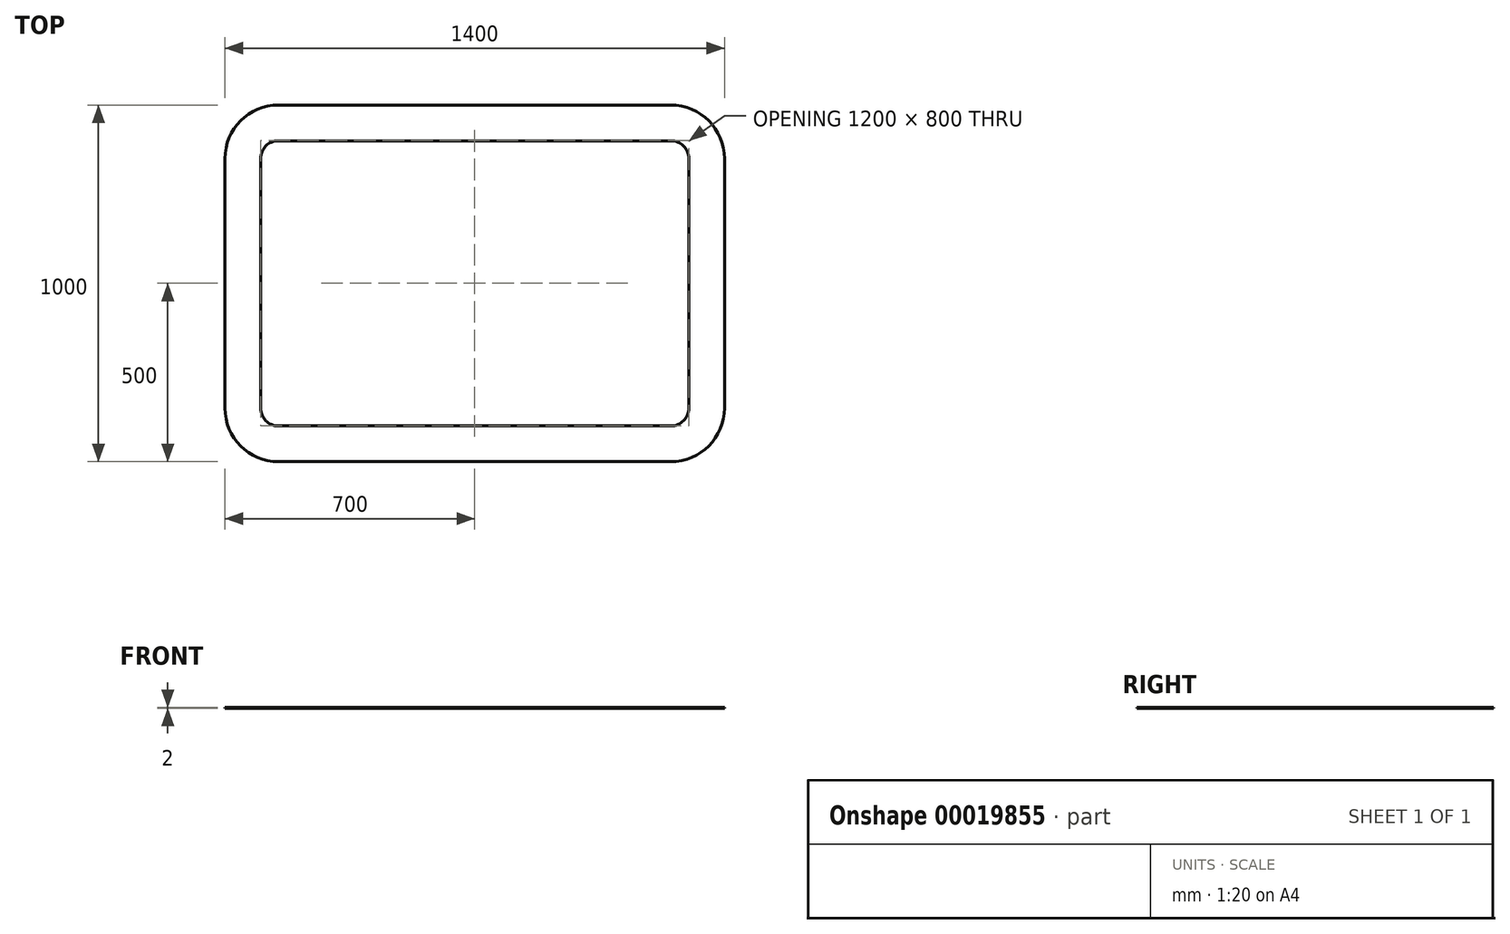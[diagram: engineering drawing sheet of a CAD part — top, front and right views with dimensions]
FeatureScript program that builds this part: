
annotation { "Feature Type Name" : "Feature", "Feature Type Description" : "" }
export const myFeature = defineFeature(function(context is Context, id is Id, definition is map)
    precondition{}
    {
        {
            var Q0;
            Q0=qCreatedBy(makeId("Top.planeOp"),FACE);
            var sketch = newSketch(context, id + "F0", { "sketchPlane" : qUnion([Q0])});
            skLineSegment(sketch, "E0.rect.bottom", {"start": v(-550, 400) * mm, "end": v(550, 400) * mm});
            skLineSegment(sketch, "E0.rect.top", {"start": v(-550, -400) * mm, "end": v(550, -400) * mm});
            skLineSegment(sketch, "E0.rect.left", {"start": v(-600, 350) * mm, "end": v(-600, -350) * mm});
            skLineSegment(sketch, "E0.rect.right", {"start": v(600, 350) * mm, "end": v(600, -350) * mm});
            skPoint(sketch, "E0.rect.middle", {"position": v(0, 0) * mm});
            skPoint(sketch, "E1.visualSharp", {"position": v(-600, 400) * mm});
            skArc(sketch, "E1.filletArc", {"start": v(-550, 400) * mm, "mid": v(-585.36, 385.36) * mm, "end": v(-600, 350) * mm});
            skPoint(sketch, "E2.visualSharp", {"position": v(-600, -400) * mm});
            skArc(sketch, "E2.filletArc", {"start": v(-600, -350) * mm, "mid": v(-585.36, -385.36) * mm, "end": v(-550, -400) * mm});
            skPoint(sketch, "E3.visualSharp", {"position": v(600, -400) * mm});
            skArc(sketch, "E3.filletArc", {"start": v(550, -400) * mm, "mid": v(585.36, -385.36) * mm, "end": v(600, -350) * mm});
            skPoint(sketch, "E4.visualSharp", {"position": v(600, 400) * mm});
            skArc(sketch, "E4.filletArc", {"start": v(600, 350) * mm, "mid": v(585.36, 385.36) * mm, "end": v(550, 400) * mm});
            skArc(sketch, "E5.0", {"start": v(-550, 500) * mm, "mid": v(-656.07, 456.07) * mm, "end": v(-700, 350) * mm});
            skLineSegment(sketch, "E5.1", {"start": v(-550, 500) * mm, "end": v(550, 500) * mm});
            skArc(sketch, "E5.2", {"start": v(700, 350) * mm, "mid": v(656.07, 456.07) * mm, "end": v(550, 500) * mm});
            skLineSegment(sketch, "E5.3", {"start": v(700, 350) * mm, "end": v(700, -350) * mm});
            skArc(sketch, "E5.4", {"start": v(550, -500) * mm, "mid": v(656.07, -456.07) * mm, "end": v(700, -350) * mm});
            skLineSegment(sketch, "E5.5", {"start": v(-700, 350) * mm, "end": v(-700, -350) * mm});
            skLineSegment(sketch, "E5.6", {"start": v(-550, -500) * mm, "end": v(550, -500) * mm});
            skArc(sketch, "E5.7", {"start": v(-700, -350) * mm, "mid": v(-656.07, -456.07) * mm, "end": v(-550, -500) * mm});
            skArc(sketch, "E6.0", {"start": v(550, -405) * mm, "mid": v(588.9, -388.9) * mm, "end": v(605, -350) * mm});
            skSolve(sketch);
        }
        {
            var Q0;
            Q0=makeQuery(id+"F0.imprint","IMPRINT",FACE,{"disambiguationData":[TD([[makeQuery(id+"F0.imprint","IMPRINT",EDGE,{"derivedFrom":sQuery(id+"F0.wireOp",EDGE,"E0.rect.top")}),-1.0]])]});
            extrude(context, id + "F1", {"entities" : qUnion([Q0]), "depth" : 2 * mm});
        }
        {
            var Q0;
            Q0=qCreatedBy(makeId("Top.planeOp"),FACE);
            cPlane(context, id + "F2", {"entities" : qUnion([Q0]), "cplaneType" : CPlaneType.OFFSET, "offset" : 100 * mm, "oppositeDirection" : true, "width" : 150 * mm, "height" : 150 * mm});
        }
        {
            var Q0;
            Q0=qCreatedBy(id+"F2.planeOp",FACE);
            var sketch = newSketch(context, id + "F3", { "sketchPlane" : qUnion([Q0])});
            skLineSegment(sketch, "E7.0", {"start": v(-550, 400) * mm, "end": v(550, 400) * mm});
            skArc(sketch, "E8.0", {"start": v(600, 350) * mm, "mid": v(585.36, 385.36) * mm, "end": v(550, 400) * mm});
            skLineSegment(sketch, "E9.0", {"start": v(600, 350) * mm, "end": v(600, -350) * mm});
            skArc(sketch, "E10.0", {"start": v(550, -400) * mm, "mid": v(585.36, -385.36) * mm, "end": v(600, -350) * mm});
            skLineSegment(sketch, "E11.0", {"start": v(-550, -400) * mm, "end": v(550, -400) * mm});
            skArc(sketch, "E12.0", {"start": v(-600, -350) * mm, "mid": v(-585.36, -385.36) * mm, "end": v(-550, -400) * mm});
            skLineSegment(sketch, "E13.0", {"start": v(-600, 350) * mm, "end": v(-600, -350) * mm});
            skArc(sketch, "E14.0", {"start": v(-550, 400) * mm, "mid": v(-585.36, 385.36) * mm, "end": v(-600, 350) * mm});
            skLineSegment(sketch, "E15.0", {"start": v(-585, 350) * mm, "end": v(-585, -350) * mm});
            skArc(sketch, "E15.1", {"start": v(-550, 385) * mm, "mid": v(-574.75, 374.75) * mm, "end": v(-585, 350) * mm});
            skLineSegment(sketch, "E15.2", {"start": v(-550, 385) * mm, "end": v(550, 385) * mm});
            skArc(sketch, "E15.3", {"start": v(585, 350) * mm, "mid": v(574.75, 374.75) * mm, "end": v(550, 385) * mm});
            skLineSegment(sketch, "E15.4", {"start": v(585, 350) * mm, "end": v(585, -350) * mm});
            skArc(sketch, "E15.5", {"start": v(-585, -350) * mm, "mid": v(-574.75, -374.75) * mm, "end": v(-550, -385) * mm});
            skArc(sketch, "E15.6", {"start": v(550, -385) * mm, "mid": v(574.75, -374.75) * mm, "end": v(585, -350) * mm});
            skLineSegment(sketch, "E15.7", {"start": v(-550, -385) * mm, "end": v(550, -385) * mm});
            skSolve(sketch);
        }
    });
